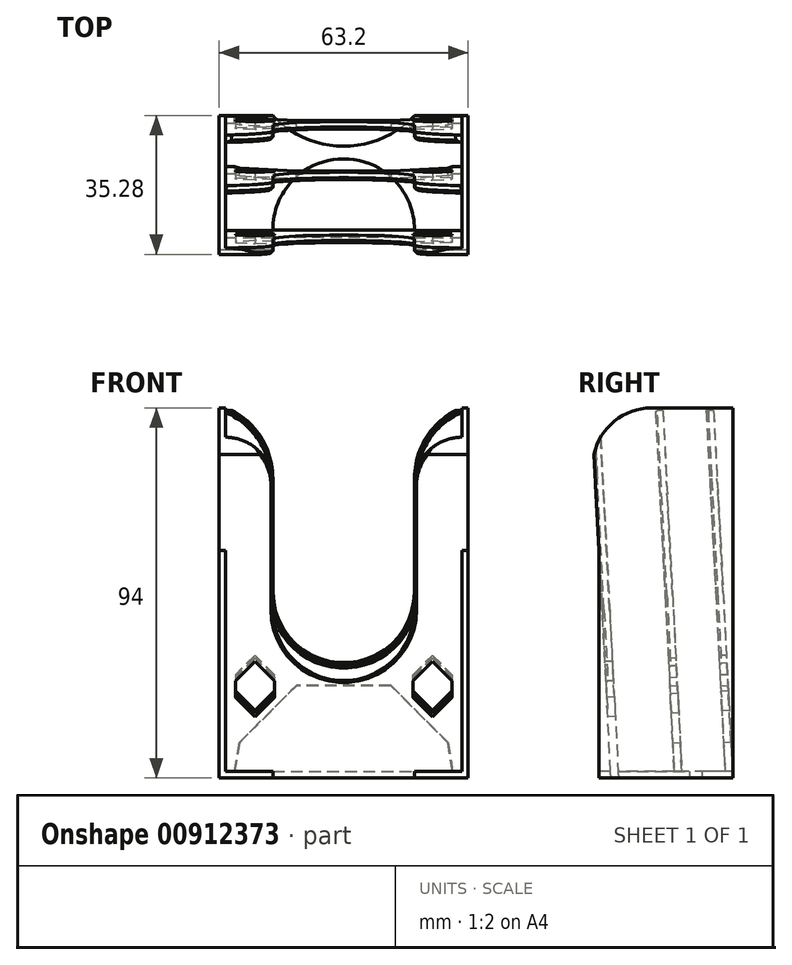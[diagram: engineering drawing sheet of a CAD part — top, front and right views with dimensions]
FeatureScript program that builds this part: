
annotation { "Feature Type Name" : "Feature", "Feature Type Description" : "" }
export const myFeature = defineFeature(function(context is Context, id is Id, definition is map)
    precondition{}
    {
        {
            assignVariable(context, id + "F0", {"name" : "wall", "anyValue" : 1.6});
        }
        {
            assignVariable(context, id + "F1", {"name" : "y", "anyValue" : 94});
        }
        {
            var Q0;
            Q0=qCreatedBy(makeId("Top.planeOp"),FACE);
            var sketch = newSketch(context, id + "F2", { "sketchPlane" : qUnion([Q0])});
            skLineSegment(sketch, "E0.bottom", {"start": v(-30, 29) * mm, "end": v(30, 29) * mm});
            skLineSegment(sketch, "E0.top", {"start": v(-30, -5) * mm, "end": v(30, -5) * mm});
            skLineSegment(sketch, "E0.left", {"start": v(-30, 29) * mm, "end": v(-30, -5) * mm});
            skLineSegment(sketch, "E0.right", {"start": v(30, 29) * mm, "end": v(30, -5) * mm});
            skArc(sketch, "E1", {"start": v(18, 0) * mm, "mid": v(0, 18) * mm, "end": v(-18, 0) * mm});
            skLineSegment(sketch, "E2", {"start": v(-18, 0) * mm, "end": v(-18, -5) * mm});
            skLineSegment(sketch, "E3", {"start": v(18, 0) * mm, "end": v(18, -5) * mm});
            skLineSegment(sketch, "E4", {"start": v(-18, 0) * mm, "end": v(-30, 0) * mm, "construction": true});
            skLineSegment(sketch, "E5", {"start": v(18, 0) * mm, "end": v(30, 0) * mm, "construction": true});
            skLineSegment(sketch, "E6.bottom", {"start": v(30, 29) * mm, "end": v(31.6, 29) * mm});
            skLineSegment(sketch, "E6.top", {"start": v(30, -5) * mm, "end": v(31.6, -5) * mm});
            skLineSegment(sketch, "E6.right", {"start": v(31.6, 29) * mm, "end": v(31.6, -5) * mm});
            skLineSegment(sketch, "E7.bottom", {"start": v(-30, 29) * mm, "end": v(-31.6, 29) * mm});
            skLineSegment(sketch, "E7.top", {"start": v(-30, -5) * mm, "end": v(-31.6, -5) * mm});
            skLineSegment(sketch, "E7.right", {"start": v(-31.6, 29) * mm, "end": v(-31.6, -5) * mm});
            skArc(sketch, "E8", {"start": v(-18, 29) * mm, "mid": v(0, 21.2) * mm, "end": v(18, 29) * mm});
            skSolve(sketch);
        }
        {
            var Q0;
            Q0=makeQuery(id+"F2.imprint","IMPRINT",FACE,{"disambiguationData":[TD([[makeQuery(id+"F2.imprint","IMPRINT",EDGE,{"derivedFrom":sQuery(id+"F2.wireOp",EDGE,"E0.bottom")}),-1.0]])]});
            extrude(context, id + "F3", {"entities" : qUnion([Q0]), "depth" : (getVariable(context, 'wall')) * mm, "offsetDistance" : 25 * mm});
        }
        {
            var Q0;
            Q0=makeQuery(id+"F2.imprint","IMPRINT",FACE,{"disambiguationData":[TD([[makeQuery(id+"F2.imprint","IMPRINT",EDGE,{"derivedFrom":sQuery(id+"F2.wireOp",EDGE,"E7.bottom")}),1.0]])]});
            var Q1;
            Q1=makeQuery(id+"F2.imprint","IMPRINT",FACE,{"disambiguationData":[TD([[makeQuery(id+"F2.imprint","IMPRINT",EDGE,{"derivedFrom":sQuery(id+"F2.wireOp",EDGE,"E6.bottom")}),-1.0]])]});
            extrude(context, id + "F4", {"entities" : qUnion([Q0, Q1]), "operationType" : NewBodyOperationType.ADD, "depth" : (getVariable(context, 'y')) * mm, "offsetDistance" : 25 * mm});
        }
        {
            var Q0;
            Q0=makeQuery(id+"F4.opExtrude","SWEPT_FACE",FACE,{"disambiguationData":[OSD([sQuery(id+"F2.wireOp",EDGE,"E7.right")])]});
            var sketch = newSketch(context, id + "F5", { "sketchPlane" : qUnion([Q0])});
            skLineSegment(sketch, "E9", {"start": v(-27.77, 23.5) * mm, "end": v(-24.07, 94) * mm});
            skLineSegment(sketch, "E10", {"start": v(-27.77, 23.5) * mm, "end": v(-25.87, 23.4) * mm});
            skLineSegment(sketch, "E11", {"start": v(-25.87, 23.4) * mm, "end": v(-22.17, 94) * mm});
            skLineSegment(sketch, "E12.1.0.0", {"start": v(-12.97, 23.4) * mm, "end": v(-9.27, 94) * mm});
            skLineSegment(sketch, "E12.1.0.1", {"start": v(-14.87, 23.5) * mm, "end": v(-11.17, 94) * mm});
            skLineSegment(sketch, "E12.direction1", {"start": v(-25.87, 23.4) * mm, "end": v(-12.97, 23.4) * mm, "construction": true});
            skLineSegment(sketch, "E13", {"start": v(-27.77, 23.5) * mm, "end": v(-29, 0) * mm, "construction": true});
            skLineSegment(sketch, "E14", {"start": v(-12.97, 23.4) * mm, "end": v(-14.87, 23.5) * mm});
            skLineSegment(sketch, "E15", {"start": v(-9.3, 93.4) * mm, "end": v(-11.2, 93.4) * mm});
            skLineSegment(sketch, "E16", {"start": v(-22.2, 93.4) * mm, "end": v(-24.1, 93.4) * mm});
            skArc(sketch, "E17", {"start": v(6.6, 79.13) * mm, "mid": v(2.25, 89.65) * mm, "end": v(-8.27, 94) * mm});
            skLineSegment(sketch, "E18", {"start": v(6.6, 79.13) * mm, "end": v(5, 79.13) * mm});
            skLineSegment(sketch, "E19", {"start": v(-8.27, 94) * mm, "end": v(-1.34, 92.29) * mm, "construction": true});
            skLineSegment(sketch, "E20", {"start": v(-1.34, 92.29) * mm, "end": v(1.74, 90.12) * mm, "construction": true});
            skLineSegment(sketch, "E21", {"start": v(1.74, 90.12) * mm, "end": v(5.43, 84.92) * mm, "construction": true});
            skLineSegment(sketch, "E22", {"start": v(5.43, 84.92) * mm, "end": v(6.6, 79.13) * mm, "construction": true});
            skPoint(sketch, "E23", {"position": v(2.25, 89.65) * mm});
            skLineSegment(sketch, "E24", {"start": v(-14.87, 23.5) * mm, "end": v(-16.1, 0) * mm, "construction": true});
            skLineSegment(sketch, "E25.1.0.0", {"start": v(1.3, 23.5) * mm, "end": v(5, 94) * mm});
            skLineSegment(sketch, "E25.1.0.1", {"start": v(3.2, 23.4) * mm, "end": v(6.9, 94) * mm});
            skLineSegment(sketch, "E25.direction1", {"start": v(-14.87, 23.5) * mm, "end": v(1.3, 23.5) * mm, "construction": true});
            skLineSegment(sketch, "E26", {"start": v(6.9, 94) * mm, "end": v(5, 94) * mm});
            skLineSegment(sketch, "E27", {"start": v(1.3, 23.5) * mm, "end": v(0.07, 0) * mm});
            skLineSegment(sketch, "E28", {"start": v(3.2, 23.4) * mm, "end": v(1.97, 0) * mm});
            skSolve(sketch);
        }
        {
            var Q0;
            {var subQ0=sQuery(id+"F5.wireOp",EDGE,"E17");var subQ1=sQuery(id+"F2.wireOp",EDGE,"E7.right");var subQ2=makeQuery(id+"F4.opExtrude","CAP_EDGE",EDGE,{"disambiguationData":[OSD([subQ1])],"isStart":false});var subQ3=makeQuery(id+"F5.imprint","INTERSECT",VERTEX,{"derivedFrom":[subQ2,subQ0]});Q0=makeQuery(id+"F5.imprint","IMPRINT",FACE,{"disambiguationData":[TD([[makeQuery(id+"F5.imprint","IMPRINT",EDGE,{"disambiguationData":[TD([[subQ3,1.0]])],"derivedFrom":subQ0}),-1.0]])]});}
            var Q1;
            {var subQ0=sQuery(id+"F5.wireOp",EDGE,"E25.1.0.0");var subQ1=sQuery(id+"F5.wireOp",EDGE,"E17");var subQ2=makeQuery(id+"F5.imprint","INTERSECT",VERTEX,{"derivedFrom":[subQ1,subQ0]});Q1=makeQuery(id+"F5.imprint","IMPRINT",FACE,{"disambiguationData":[TD([[makeQuery(id+"F5.imprint","IMPRINT",EDGE,{"disambiguationData":[TD([[subQ2,1.0]])],"derivedFrom":subQ1}),-1.0]])]});}
            extrude(context, id + "F6", {"entities" : qUnion([Q0, Q1]), "operationType" : NewBodyOperationType.REMOVE, "endBound" : BoundingType.THROUGH_ALL, "oppositeDirection" : true, "depth" : 25 * mm, "offsetDistance" : 25 * mm});
        }
        {
            var Q0;
            {var subQ0=sQuery(id+"F5.wireOp",EDGE,"E14");Q0=makeQuery(id+"F5.imprint","IMPRINT",FACE,{"disambiguationData":[TD([[makeQuery(id+"F5.imprint","IMPRINT",EDGE,{"derivedFrom":subQ0}),-1.0]])]});}
            var Q1;
            {var subQ0=sQuery(id+"F5.wireOp",EDGE,"E10");Q1=makeQuery(id+"F5.imprint","IMPRINT",FACE,{"disambiguationData":[TD([[makeQuery(id+"F5.imprint","IMPRINT",EDGE,{"derivedFrom":subQ0}),1.0]])]});}
            var Q2;
            {var subQ0=sQuery(id+"F5.wireOp",EDGE,"E27");Q2=makeQuery(id+"F5.imprint","IMPRINT",FACE,{"disambiguationData":[TD([[makeQuery(id+"F5.imprint","IMPRINT",EDGE,{"derivedFrom":subQ0}),1.0]])]});}
            var Q3;
            {var subQ3=sQuery(id+"F5.wireOp",EDGE,"E22");var subQ5=sQuery(id+"F5.wireOp",EDGE,"E21");var subQ6=makeQuery(id+"F5.imprint","INTERSECT",VERTEX,{"derivedFrom":[subQ5,subQ3]});Q3=makeQuery(id+"F5.imprint","IMPRINT",FACE,{"disambiguationData":[TD([[makeQuery(id+"F5.imprint","IMPRINT",EDGE,{"disambiguationData":[TD([[subQ6,-1.0]])],"derivedFrom":subQ3}),-1.0]])]});}
            var Q4;
            {var subQ0=sQuery(id+"F5.wireOp",EDGE,"E18");var subQ3=sQuery(id+"F5.wireOp",EDGE,"E25.1.0.1");var subQ4=makeQuery(id+"F5.imprint","INTERSECT",VERTEX,{"derivedFrom":[subQ0,subQ3]});Q4=makeQuery(id+"F5.imprint","IMPRINT",FACE,{"disambiguationData":[TD([[makeQuery(id+"F5.imprint","IMPRINT",EDGE,{"disambiguationData":[TD([[subQ4,-1.0]])],"derivedFrom":subQ0}),1.0]])]});}
            var Q5;
            {var subQ0=sQuery(id+"F5.wireOp",EDGE,"E25.1.0.1");var subQ1=sQuery(id+"F5.wireOp",EDGE,"E17");var subQ2=makeQuery(id+"F5.imprint","INTERSECT",VERTEX,{"derivedFrom":[subQ1,subQ0]});Q5=makeQuery(id+"F5.imprint","IMPRINT",FACE,{"disambiguationData":[TD([[makeQuery(id+"F5.imprint","IMPRINT",EDGE,{"disambiguationData":[TD([[subQ2,1.0]])],"derivedFrom":subQ0}),1.0]])]});}
            var Q6;
            Q6=makeQuery(id+"F4.opExtrude","SWEPT_FACE",FACE,{"disambiguationData":[OSD([sQuery(id+"F2.wireOp",EDGE,"E6.right")])]});
            extrude(context, id + "F7", {"entities" : qUnion([Q0, Q1, Q2, Q3, Q4, Q5]), "operationType" : NewBodyOperationType.ADD, "endBound" : BoundingType.UP_TO_SURFACE, "oppositeDirection" : true, "depth" : 25 * mm, "endBoundEntityFace" : qUnion([Q6]), "offsetDistance" : 25 * mm});
        }
        {
            var Q0;
            {var subQ0=sQuery(id+"F2.wireOp",EDGE,"E6.top");var subQ1=sQuery(id+"F2.wireOp",EDGE,"E0.top");Q0=makeQuery(id+"F4.boolean.opBoolean","MERGE",FACE,{"derivedFrom":[makeQuery(id+"F3.opExtrude","SWEPT_FACE",FACE,{"disambiguationData":[OSD([subQ1]),TDD([makeQuery(id+"F2.imprint","IMPRINT",EDGE,{"disambiguationData":[TD([[makeQuery(id+"F2.imprint","INTERSECT",VERTEX,{"derivedFrom":[subQ1,sQuery(id+"F2.wireOp",EDGE,"E3")]}),-1.0]])],"derivedFrom":subQ1})])]}),makeQuery(id+"F4.opExtrude","SWEPT_FACE",FACE,{"disambiguationData":[OSD([subQ0])]})]});}
            var sketch = newSketch(context, id + "F8", { "sketchPlane" : qUnion([Q0])});
            skLineSegment(sketch, "E29.bottom", {"start": v(31.6, 0) * mm, "end": v(-31.6, 0) * mm});
            skLineSegment(sketch, "E29.top", {"start": v(31.6, 86.56) * mm, "end": v(-31.6, 86.56) * mm});
            skLineSegment(sketch, "E29.left", {"start": v(31.6, 0) * mm, "end": v(31.6, 86.56) * mm});
            skLineSegment(sketch, "E29.right", {"start": v(-31.6, 0) * mm, "end": v(-31.6, 86.56) * mm});
            skLineSegment(sketch, "E30.bottom", {"start": v(18, 74.56) * mm, "end": v(-18, 74.56) * mm, "construction": true});
            skLineSegment(sketch, "E30.top", {"start": v(18, 42.73) * mm, "end": v(-18, 42.73) * mm, "construction": true});
            skLineSegment(sketch, "E30.left", {"start": v(18, 74.56) * mm, "end": v(18, 42.73) * mm});
            skLineSegment(sketch, "E30.right", {"start": v(-18, 74.56) * mm, "end": v(-18, 42.73) * mm});
            skArc(sketch, "E31", {"start": v(-18, 42.73) * mm, "mid": v(0, 24.73) * mm, "end": v(18, 42.73) * mm});
            skLineSegment(sketch, "E32.bottom", {"start": v(18, 0) * mm, "end": v(-18, 0) * mm});
            skLineSegment(sketch, "E32.top", {"start": v(18, 1.6) * mm, "end": v(-18, 1.6) * mm, "construction": true});
            skLineSegment(sketch, "E32.left", {"start": v(18, 0) * mm, "end": v(18, 1.6) * mm});
            skLineSegment(sketch, "E32.right", {"start": v(-18, 0) * mm, "end": v(-18, 1.6) * mm});
            skPoint(sketch, "E33", {"position": v(0, 0) * mm});
            skArc(sketch, "E34", {"start": v(30, 86.56) * mm, "mid": v(21.51, 83.05) * mm, "end": v(18, 74.56) * mm});
            skLineSegment(sketch, "E35", {"start": v(0, 42.73) * mm, "end": v(0, 74.56) * mm, "construction": true});
            skArc(sketch, "E36.MirrorCS", {"start": v(-30, 86.56) * mm, "mid": v(-21.51, 83.05) * mm, "end": v(-18, 74.56) * mm});
            skCircle(sketch, "E37.cCircle", {"center": v(0, 1.6) * mm, "radius": 17.12 * mm, "construction": true});
            skLineSegment(sketch, "E37.0", {"start": v(-5.56, 18.72) * mm, "end": v(5.56, 18.72) * mm});
            skLineSegment(sketch, "E37.1", {"start": v(5.56, 18.72) * mm, "end": v(14.56, 12.18) * mm});
            skLineSegment(sketch, "E37.2", {"start": v(14.56, 12.18) * mm, "end": v(18, 1.6) * mm});
            skLineSegment(sketch, "E37.3", {"start": v(18, 1.6) * mm, "end": v(14.56, -8.98) * mm, "construction": true});
            skLineSegment(sketch, "E37.4", {"start": v(14.56, -8.98) * mm, "end": v(5.56, -15.52) * mm});
            skLineSegment(sketch, "E37.5", {"start": v(5.56, -15.52) * mm, "end": v(-5.56, -15.52) * mm});
            skLineSegment(sketch, "E37.6", {"start": v(-5.56, -15.52) * mm, "end": v(-14.56, -8.98) * mm});
            skLineSegment(sketch, "E37.7", {"start": v(-14.56, -8.98) * mm, "end": v(-18, 1.6) * mm, "construction": true});
            skLineSegment(sketch, "E37.8", {"start": v(-18, 1.6) * mm, "end": v(-14.56, 12.18) * mm});
            skLineSegment(sketch, "E37.9", {"start": v(-14.56, 12.18) * mm, "end": v(-5.56, 18.72) * mm});
            skPoint(sketch, "E37.0.midPoint", {"position": v(0, 18.72) * mm});
            skCircle(sketch, "E38.cCircle", {"center": v(20.4, 21.48) * mm, "radius": 6.6 * mm, "construction": true});
            skLineSegment(sketch, "E38.0", {"start": v(13.8, 17.68) * mm, "end": v(13.8, 25.3) * mm});
            skLineSegment(sketch, "E38.1", {"start": v(13.8, 25.3) * mm, "end": v(20.4, 29.1) * mm});
            skLineSegment(sketch, "E38.2", {"start": v(20.4, 29.1) * mm, "end": v(27, 25.3) * mm});
            skLineSegment(sketch, "E38.3", {"start": v(27, 25.3) * mm, "end": v(27, 17.68) * mm});
            skLineSegment(sketch, "E38.4", {"start": v(27, 17.68) * mm, "end": v(20.4, 13.87) * mm});
            skLineSegment(sketch, "E38.5", {"start": v(20.4, 13.87) * mm, "end": v(13.8, 17.68) * mm});
            skPoint(sketch, "E38.0.midPoint", {"position": v(13.8, 21.48) * mm});
            skLineSegment(sketch, "E39", {"start": v(0, 18.72) * mm, "end": v(0, 24.73) * mm, "construction": true});
            skLineSegment(sketch, "E40.MirrorCS", {"start": v(-13.8, 17.68) * mm, "end": v(-13.8, 25.3) * mm});
            skLineSegment(sketch, "E41.MirrorCS", {"start": v(-20.4, 13.87) * mm, "end": v(-13.8, 17.68) * mm});
            skLineSegment(sketch, "E42.MirrorCS", {"start": v(-27, 17.68) * mm, "end": v(-20.4, 13.87) * mm});
            skLineSegment(sketch, "E43.MirrorCS", {"start": v(-27, 25.3) * mm, "end": v(-27, 17.68) * mm});
            skLineSegment(sketch, "E44.MirrorCS", {"start": v(-20.4, 29.1) * mm, "end": v(-27, 25.3) * mm});
            skLineSegment(sketch, "E45.MirrorCS", {"start": v(-13.8, 25.3) * mm, "end": v(-20.4, 29.1) * mm});
            skPoint(sketch, "E46.0", {"position": v(30, 86.56) * mm});
            skPoint(sketch, "E46.1", {"position": v(-30, 86.56) * mm});
            skSolve(sketch);
        }
        {
            var Q0;
            Q0=makeQuery(id+"F8.imprint","IMPRINT",FACE,{"disambiguationData":[TD([[makeQuery(id+"F8.imprint","IMPRINT",EDGE,{"derivedFrom":sQuery(id+"F8.wireOp",EDGE,"E30.left")}),-1.0]])]});
            var Q1;
            Q1=makeQuery(id+"F8.imprint","IMPRINT",FACE,{"disambiguationData":[TD([[makeQuery(id+"F8.imprint","IMPRINT",EDGE,{"derivedFrom":sQuery(id+"F8.wireOp",EDGE,"E32.bottom")}),-1.0]])]});
            extrude(context, id + "F9", {"entities" : qUnion([Q0, Q1]), "operationType" : NewBodyOperationType.REMOVE, "depth" : 5 * mm, "offsetDistance" : 25 * mm, "hasSecondDirection" : true, "secondDirectionOppositeDirection" : true, "secondDirectionDepth" : 5 * mm});
        }
        {
            var Q0;
            {var subQ5=sQuery(id+"F8.wireOp",EDGE,"E29.right");Q0=makeQuery(id+"F8.imprint","IMPRINT",FACE,{"disambiguationData":[TD([[makeQuery(id+"F8.imprint","IMPRINT",EDGE,{"derivedFrom":subQ5}),-1.0]])]});}
            var sketch = newSketch(context, id + "F10", { "sketchPlane" : qUnion([Q0])});
            skArc(sketch, "E47.0.0", {"start": v(-18, 74.56) * mm, "mid": v(-21.51, 83.05) * mm, "end": v(-30, 86.56) * mm});
            skArc(sketch, "E47.0.5", {"start": v(-18, 1.6) * mm, "mid": v(0, 20.88) * mm, "end": v(18, 1.6) * mm});
            skLineSegment(sketch, "E47.0.6", {"start": v(18, 1.6) * mm, "end": v(30, 1.6) * mm});
            skLineSegment(sketch, "E47.0.7", {"start": v(30, 1.6) * mm, "end": v(30, 57.75) * mm});
            skArc(sketch, "E47.0.8", {"start": v(30, 86.56) * mm, "mid": v(21.51, 83.05) * mm, "end": v(18, 74.56) * mm});
            skLineSegment(sketch, "E47.0.9", {"start": v(18, 74.56) * mm, "end": v(18, 42.73) * mm});
            skArc(sketch, "E47.0.10", {"start": v(18, 42.73) * mm, "mid": v(0, 24.73) * mm, "end": v(-18, 42.73) * mm});
            skLineSegment(sketch, "E47.0.11", {"start": v(-18, 42.73) * mm, "end": v(-18, 74.56) * mm});
            skLineSegment(sketch, "E47.1.2", {"start": v(30, 57.75) * mm, "end": v(30, 1.6) * mm});
            skLineSegment(sketch, "E47.1.3", {"start": v(30, 1.6) * mm, "end": v(18, 1.6) * mm});
            skLineSegment(sketch, "E48", {"start": v(-18, 1.6) * mm, "end": v(-30, 1.6) * mm});
            skLineSegment(sketch, "E49", {"start": v(-30, 1.6) * mm, "end": v(-30, 86.56) * mm});
            skPoint(sketch, "E47.0.2.start.orphan", {"position": v(-31.6, 86.56) * mm});
            skPoint(sketch, "E47.0.3.start.orphan", {"position": v(-31.6, 0) * mm});
            skPoint(sketch, "E47.0.4.start.orphan", {"position": v(-18, 0) * mm});
            skPoint(sketch, "E47.1.5.start.orphan", {"position": v(18, 0) * mm});
            skPoint(sketch, "E47.1.0.start.orphan", {"position": v(31.6, 0) * mm});
            skPoint(sketch, "E47.1.1.start.orphan", {"position": v(31.6, 57.75) * mm});
            skLineSegment(sketch, "E50", {"start": v(31.6, 57.75) * mm, "end": v(30, 57.75) * mm});
            skLineSegment(sketch, "E51", {"start": v(-30, 86.56) * mm, "end": v(-31.6, 86.56) * mm});
            skLineSegment(sketch, "E52", {"start": v(-31.6, 86.56) * mm, "end": v(-31.6, 39.56) * mm});
            skLineSegment(sketch, "E53", {"start": v(-31.6, 39.56) * mm, "end": v(-30, 39.56) * mm});
            skLineSegment(sketch, "E54", {"start": v(31.6, 57.75) * mm, "end": v(31.6, 39.56) * mm});
            skLineSegment(sketch, "E55", {"start": v(31.6, 39.56) * mm, "end": v(30, 39.56) * mm});
            skSolve(sketch);
        }
        {
            var Q0;
            Q0=makeQuery(id+"F7.boolean.opBoolean","INTERSECT",EDGE,{"derivedFrom":[makeQuery(id+"F4.opExtrude","SWEPT_FACE",FACE,{"disambiguationData":[OSD([sQuery(id+"F2.wireOp",EDGE,"E0.right")])]}),makeQuery(id+"F7.opExtrude","SWEPT_FACE",FACE,{"disambiguationData":[OSD([sQuery(id+"F5.wireOp",EDGE,"E10")])]})]});
            var Q1;
            Q1=makeQuery(id+"F7.boolean.opBoolean","INTERSECT",EDGE,{"derivedFrom":[makeQuery(id+"F4.opExtrude","SWEPT_FACE",FACE,{"disambiguationData":[OSD([sQuery(id+"F2.wireOp",EDGE,"E0.right")])]}),makeQuery(id+"F7.opExtrude","SWEPT_FACE",FACE,{"disambiguationData":[OSD([sQuery(id+"F5.wireOp",EDGE,"E14")])]})]});
            var Q2;
            Q2=makeQuery(id+"F7.boolean.opBoolean","INTERSECT",EDGE,{"derivedFrom":[makeQuery(id+"F4.opExtrude","SWEPT_FACE",FACE,{"disambiguationData":[OSD([sQuery(id+"F2.wireOp",EDGE,"E0.left")])]}),makeQuery(id+"F7.opExtrude","SWEPT_FACE",FACE,{"disambiguationData":[OSD([sQuery(id+"F5.wireOp",EDGE,"E14")])]})]});
            var Q3;
            Q3=makeQuery(id+"F7.boolean.opBoolean","INTERSECT",EDGE,{"derivedFrom":[makeQuery(id+"F4.opExtrude","SWEPT_FACE",FACE,{"disambiguationData":[OSD([sQuery(id+"F2.wireOp",EDGE,"E0.left")])]}),makeQuery(id+"F7.opExtrude","SWEPT_FACE",FACE,{"disambiguationData":[OSD([sQuery(id+"F5.wireOp",EDGE,"E10")])]})]});
            chamfer(context, id + "F11", {"entities" : qUnion([Q0, Q1, Q2, Q3]), "width" : 18 * mm, "tangentPropagation" : true});
        }
        {
            var Q0;
            {var subQ0=makeQuery(id+"F4.opExtrude","SWEPT_FACE",FACE,{"disambiguationData":[OSD([sQuery(id+"F2.wireOp",EDGE,"E0.left")])]});Q0=makeQuery(id+"F11.opChamfer","BLEND_EDGE",EDGE,{"blendedFrom":[makeQuery(id+"F7.boolean.opBoolean","INTERSECT",EDGE,{"derivedFrom":[subQ0,makeQuery(id+"F7.opExtrude","SWEPT_FACE",FACE,{"disambiguationData":[OSD([sQuery(id+"F5.wireOp",EDGE,"E10")])]})]}),makeQuery(id+"F6aKBNFIJvLf6Fg_2.boolean.opBoolean","MERGE",FACE,{"derivedFrom":[subQ0,makeQuery(id+"F6aKBNFIJvLf6Fg_2.opExtrude","CAP_FACE",FACE,{"disambiguationData":[OSD([sQuery(id+"F2.wireOp",EDGE,"E7.top"),sQuery(id+"F2.wireOp",EDGE,"E7.right"),sQuery(id+"F5.wireOp",EDGE,"E18"),sQuery(id+"F5.wireOp",EDGE,"E21"),sQuery(id+"F5.wireOp",EDGE,"E22")])],"isStart":false})]})],"blendedInto":[makeQuery(id+"F6aKBNFIJvLf6Fg_2.boolean.opBoolean","MERGE",FACE,{"derivedFrom":[subQ0,makeQuery(id+"F6aKBNFIJvLf6Fg_2.opExtrude","CAP_FACE",FACE,{"disambiguationData":[OSD([sQuery(id+"F2.wireOp",EDGE,"E7.top"),sQuery(id+"F2.wireOp",EDGE,"E7.right"),sQuery(id+"F5.wireOp",EDGE,"E18"),sQuery(id+"F5.wireOp",EDGE,"E21"),sQuery(id+"F5.wireOp",EDGE,"E22")])],"isStart":false})]})]});}
            var Q1;
            {var subQ0=makeQuery(id+"F4.opExtrude","SWEPT_FACE",FACE,{"disambiguationData":[OSD([sQuery(id+"F2.wireOp",EDGE,"E0.left")])]});Q1=makeQuery(id+"F11.opChamfer","BLEND_EDGE",EDGE,{"blendedFrom":[makeQuery(id+"F7.boolean.opBoolean","INTERSECT",EDGE,{"derivedFrom":[subQ0,makeQuery(id+"F7.opExtrude","SWEPT_FACE",FACE,{"disambiguationData":[OSD([sQuery(id+"F5.wireOp",EDGE,"E14")])]})]}),makeQuery(id+"F6aKBNFIJvLf6Fg_2.boolean.opBoolean","MERGE",FACE,{"derivedFrom":[subQ0,makeQuery(id+"F6aKBNFIJvLf6Fg_2.opExtrude","CAP_FACE",FACE,{"disambiguationData":[OSD([sQuery(id+"F2.wireOp",EDGE,"E7.top"),sQuery(id+"F2.wireOp",EDGE,"E7.right"),sQuery(id+"F5.wireOp",EDGE,"E18"),sQuery(id+"F5.wireOp",EDGE,"E21"),sQuery(id+"F5.wireOp",EDGE,"E22")])],"isStart":false})]})],"blendedInto":[makeQuery(id+"F6aKBNFIJvLf6Fg_2.boolean.opBoolean","MERGE",FACE,{"derivedFrom":[subQ0,makeQuery(id+"F6aKBNFIJvLf6Fg_2.opExtrude","CAP_FACE",FACE,{"disambiguationData":[OSD([sQuery(id+"F2.wireOp",EDGE,"E7.top"),sQuery(id+"F2.wireOp",EDGE,"E7.right"),sQuery(id+"F5.wireOp",EDGE,"E18"),sQuery(id+"F5.wireOp",EDGE,"E21"),sQuery(id+"F5.wireOp",EDGE,"E22")])],"isStart":false})]})]});}
            var Q2;
            {var subQ0=makeQuery(id+"F4.opExtrude","SWEPT_FACE",FACE,{"disambiguationData":[OSD([sQuery(id+"F2.wireOp",EDGE,"E0.right")])]});Q2=makeQuery(id+"F11.opChamfer","BLEND_EDGE",EDGE,{"blendedFrom":[makeQuery(id+"F7.boolean.opBoolean","INTERSECT",EDGE,{"derivedFrom":[subQ0,makeQuery(id+"F7.opExtrude","SWEPT_FACE",FACE,{"disambiguationData":[OSD([sQuery(id+"F5.wireOp",EDGE,"E14")])]})]}),makeQuery(id+"F94SPbiB62YBjDw_1.boolean.opBoolean","MERGE",FACE,{"derivedFrom":[subQ0,makeQuery(id+"F94SPbiB62YBjDw_1.opExtrude","CAP_FACE",FACE,{"disambiguationData":[OSD([sQuery(id+"F2.wireOp",EDGE,"E7.top"),sQuery(id+"F2.wireOp",EDGE,"E7.right"),sQuery(id+"F5.wireOp",EDGE,"E18"),sQuery(id+"F5.wireOp",EDGE,"E21"),sQuery(id+"F5.wireOp",EDGE,"E22")])],"isStart":true})]})],"blendedInto":[makeQuery(id+"F94SPbiB62YBjDw_1.boolean.opBoolean","MERGE",FACE,{"derivedFrom":[subQ0,makeQuery(id+"F94SPbiB62YBjDw_1.opExtrude","CAP_FACE",FACE,{"disambiguationData":[OSD([sQuery(id+"F2.wireOp",EDGE,"E7.top"),sQuery(id+"F2.wireOp",EDGE,"E7.right"),sQuery(id+"F5.wireOp",EDGE,"E18"),sQuery(id+"F5.wireOp",EDGE,"E21"),sQuery(id+"F5.wireOp",EDGE,"E22")])],"isStart":true})]})]});}
            var Q3;
            {var subQ0=makeQuery(id+"F4.opExtrude","SWEPT_FACE",FACE,{"disambiguationData":[OSD([sQuery(id+"F2.wireOp",EDGE,"E0.right")])]});Q3=makeQuery(id+"F11.opChamfer","BLEND_EDGE",EDGE,{"blendedFrom":[makeQuery(id+"F7.boolean.opBoolean","INTERSECT",EDGE,{"derivedFrom":[subQ0,makeQuery(id+"F7.opExtrude","SWEPT_FACE",FACE,{"disambiguationData":[OSD([sQuery(id+"F5.wireOp",EDGE,"E10")])]})]}),makeQuery(id+"F94SPbiB62YBjDw_1.boolean.opBoolean","MERGE",FACE,{"derivedFrom":[subQ0,makeQuery(id+"F94SPbiB62YBjDw_1.opExtrude","CAP_FACE",FACE,{"disambiguationData":[OSD([sQuery(id+"F2.wireOp",EDGE,"E7.top"),sQuery(id+"F2.wireOp",EDGE,"E7.right"),sQuery(id+"F5.wireOp",EDGE,"E18"),sQuery(id+"F5.wireOp",EDGE,"E21"),sQuery(id+"F5.wireOp",EDGE,"E22")])],"isStart":true})]})],"blendedInto":[makeQuery(id+"F94SPbiB62YBjDw_1.boolean.opBoolean","MERGE",FACE,{"derivedFrom":[subQ0,makeQuery(id+"F94SPbiB62YBjDw_1.opExtrude","CAP_FACE",FACE,{"disambiguationData":[OSD([sQuery(id+"F2.wireOp",EDGE,"E7.top"),sQuery(id+"F2.wireOp",EDGE,"E7.right"),sQuery(id+"F5.wireOp",EDGE,"E18"),sQuery(id+"F5.wireOp",EDGE,"E21"),sQuery(id+"F5.wireOp",EDGE,"E22")])],"isStart":true})]})]});}
            chamfer(context, id + "F12", {"entities" : qUnion([Q0, Q1, Q2, Q3]), "chamferType" : ChamferType.TWO_OFFSETS, "width1" : 18 * mm, "oppositeDirection" : false, "width2" : 5 * mm, "tangentPropagation" : true});
        }
        {
            var Q0;
            Q0=makeQuery(id+"F7.opExtrude","SWEPT_FACE",FACE,{"disambiguationData":[OSD([sQuery(id+"F5.wireOp",EDGE,"E12.1.0.0")])]});
            var sketch = newSketch(context, id + "F13", { "sketchPlane" : qUnion([Q0])});
            skEllipticalArc(sketch, "E56.0", {"construction": true});
            skLineSegment(sketch, "E56.1", {"start": v(-18, 42.93) * mm, "end": v(-18, 74.72) * mm});
            skEllipticalArc(sketch, "E56.2", {});
            skLineSegment(sketch, "E56.3", {"start": v(18, 74.72) * mm, "end": v(18, 42.93) * mm});
            skEllipticalArc(sketch, "E56.4", {});
            skArc(sketch, "E57", {"start": v(-18, 45.69) * mm, "mid": v(0, 27.69) * mm, "end": v(18, 45.69) * mm});
            skArc(sketch, "E58", {"start": v(30, 92.79) * mm, "mid": v(21.27, 85.57) * mm, "end": v(18, 74.72) * mm});
            skArc(sketch, "E59", {"start": v(-18, 74.72) * mm, "mid": v(-21.27, 85.57) * mm, "end": v(-30, 92.79) * mm});
            skCircle(sketch, "E60.cCircle", {"center": v(22.54, 22.69) * mm, "radius": 4.96 * mm, "construction": true});
            skLineSegment(sketch, "E60.0", {"start": v(27.5, 24.74) * mm, "end": v(27.5, 20.64) * mm});
            skLineSegment(sketch, "E60.1", {"start": v(27.5, 20.64) * mm, "end": v(22.54, 15.68) * mm});
            skLineSegment(sketch, "E60.2", {"start": v(22.54, 15.68) * mm, "end": v(17.59, 20.64) * mm});
            skLineSegment(sketch, "E60.3", {"start": v(17.59, 20.64) * mm, "end": v(17.59, 24.74) * mm});
            skLineSegment(sketch, "E60.4", {"start": v(17.59, 24.74) * mm, "end": v(22.54, 29.7) * mm});
            skLineSegment(sketch, "E60.5", {"start": v(22.54, 29.7) * mm, "end": v(27.5, 24.74) * mm});
            skPoint(sketch, "E60.0.midPoint", {"position": v(27.5, 22.69) * mm});
            skLineSegment(sketch, "E61", {"start": v(0, 22.69) * mm, "end": v(0, 27.69) * mm, "construction": true});
            skLineSegment(sketch, "E62.MirrorCS", {"start": v(-17.59, 20.64) * mm, "end": v(-17.59, 24.74) * mm});
            skLineSegment(sketch, "E63.MirrorCS", {"start": v(-17.59, 24.74) * mm, "end": v(-22.54, 29.7) * mm});
            skLineSegment(sketch, "E64.MirrorCS", {"start": v(-22.54, 29.7) * mm, "end": v(-27.5, 24.74) * mm});
            skLineSegment(sketch, "E65.MirrorCS", {"start": v(-22.54, 15.68) * mm, "end": v(-17.59, 20.64) * mm});
            skLineSegment(sketch, "E66.MirrorCS", {"start": v(-27.5, 20.64) * mm, "end": v(-22.54, 15.68) * mm});
            skLineSegment(sketch, "E67.MirrorCS", {"start": v(-27.5, 24.74) * mm, "end": v(-27.5, 20.64) * mm});
            const initialGuessF13  = {"E56.0": [0, 0.04298273222242581, -1, 0, 0.018, 0.01797533162558233, 0, 3.141592653589793], "E56.2": [-0.03, 0.0743220685268947, 1, 0, 0.012, 0.011983554417054882, 0, 1.5707963267948966], "E56.4": [0.03, 0.0743220685268947, 1, 0, 0.012, 0.011983554417054882, 1.5707963267948966, 3.141592653589793]};
            skSetInitialGuess(sketch, initialGuessF13);
            skSolve(sketch);
        }
        {
            var Q0;
            {var subQ0=sQuery(id+"F13.wireOp",EDGE,"E57");Q0=makeQuery(id+"F13.imprint","IMPRINT",FACE,{"disambiguationData":[TD([[makeQuery(id+"F13.imprint","IMPRINT",EDGE,{"derivedFrom":subQ0}),1.0]])]});}
            var Q1;
            Q1=makeQuery(id+"F13.imprint","IMPRINT",FACE,{"disambiguationData":[TD([[makeQuery(id+"F13.imprint","IMPRINT",EDGE,{"derivedFrom":sQuery(id+"F13.wireOp",EDGE,"E60.0")}),-1.0]])]});
            var Q2;
            Q2=makeQuery(id+"F13.imprint","IMPRINT",FACE,{"disambiguationData":[TD([[makeQuery(id+"F13.imprint","IMPRINT",EDGE,{"derivedFrom":sQuery(id+"F13.wireOp",EDGE,"E62.MirrorCS")}),1.0]])]});
            extrude(context, id + "F14", {"entities" : qUnion([Q0, Q1, Q2]), "operationType" : NewBodyOperationType.REMOVE, "oppositeDirection" : true, "depth" : 25 * mm, "offsetDistance" : 25 * mm, "hasSecondDirection" : true, "secondDirectionOppositeDirection" : false, "secondDirectionDepth" : 25 * mm});
        }
        {
            var Q0;
            Q0=makeQuery(id+"F14.boolean.opBoolean","INTERSECT",EDGE,{"derivedFrom":[makeQuery(id+"F7.opExtrude","SWEPT_FACE",FACE,{"disambiguationData":[OSD([sQuery(id+"F5.wireOp",EDGE,"E12.1.0.0")])]}),makeQuery(id+"F14.opExtrude","SWEPT_FACE",FACE,{"disambiguationData":[OSD([sQuery(id+"F13.wireOp",EDGE,"E58")])]})]});
            var Q1;
            Q1=makeQuery(id+"F14.boolean.opBoolean","INTERSECT",EDGE,{"derivedFrom":[makeQuery(id+"F7.opExtrude","SWEPT_FACE",FACE,{"disambiguationData":[OSD([sQuery(id+"F5.wireOp",EDGE,"E11")])]}),makeQuery(id+"F14.opExtrude","SWEPT_FACE",FACE,{"disambiguationData":[OSD([sQuery(id+"F13.wireOp",EDGE,"E58")])]})]});
            var Q2;
            Q2=makeQuery(id+"F9.boolean.opBoolean","INTERSECT",EDGE,{"derivedFrom":[makeQuery(id+"F7.opExtrude","SWEPT_FACE",FACE,{"disambiguationData":[OSD([sQuery(id+"F5.wireOp",EDGE,"E25.1.0.1"),sQuery(id+"F5.wireOp",EDGE,"E28")])]}),makeQuery(id+"F9.opExtrude","SWEPT_FACE",FACE,{"disambiguationData":[OSD([sQuery(id+"F8.wireOp",EDGE,"E34")])]})]});
            var Q3;
            Q3=makeQuery(id+"F9.boolean.opBoolean","INTERSECT",EDGE,{"derivedFrom":[makeQuery(id+"F7.opExtrude","SWEPT_FACE",FACE,{"disambiguationData":[OSD([sQuery(id+"F5.wireOp",EDGE,"E25.1.0.1"),sQuery(id+"F5.wireOp",EDGE,"E28")])]}),makeQuery(id+"F9.opExtrude","SWEPT_FACE",FACE,{"disambiguationData":[OSD([sQuery(id+"F8.wireOp",EDGE,"E36.MirrorCS")])]})]});
            var Q4;
            Q4=makeQuery(id+"F14.boolean.opBoolean","INTERSECT",EDGE,{"derivedFrom":[makeQuery(id+"F7.opExtrude","SWEPT_FACE",FACE,{"disambiguationData":[OSD([sQuery(id+"F5.wireOp",EDGE,"E12.1.0.0")])]}),makeQuery(id+"F14.opExtrude","SWEPT_FACE",FACE,{"disambiguationData":[OSD([sQuery(id+"F13.wireOp",EDGE,"E59")])]})]});
            var Q5;
            Q5=makeQuery(id+"F14.boolean.opBoolean","INTERSECT",EDGE,{"derivedFrom":[makeQuery(id+"F7.opExtrude","SWEPT_FACE",FACE,{"disambiguationData":[OSD([sQuery(id+"F5.wireOp",EDGE,"E11")])]}),makeQuery(id+"F14.opExtrude","SWEPT_FACE",FACE,{"disambiguationData":[OSD([sQuery(id+"F13.wireOp",EDGE,"E59")])]})]});
            chamfer(context, id + "F15", {"entities" : qUnion([Q0, Q1, Q2, Q3, Q4, Q5]), "width" : 0.5 * mm, "tangentPropagation" : true});
        }
    });
